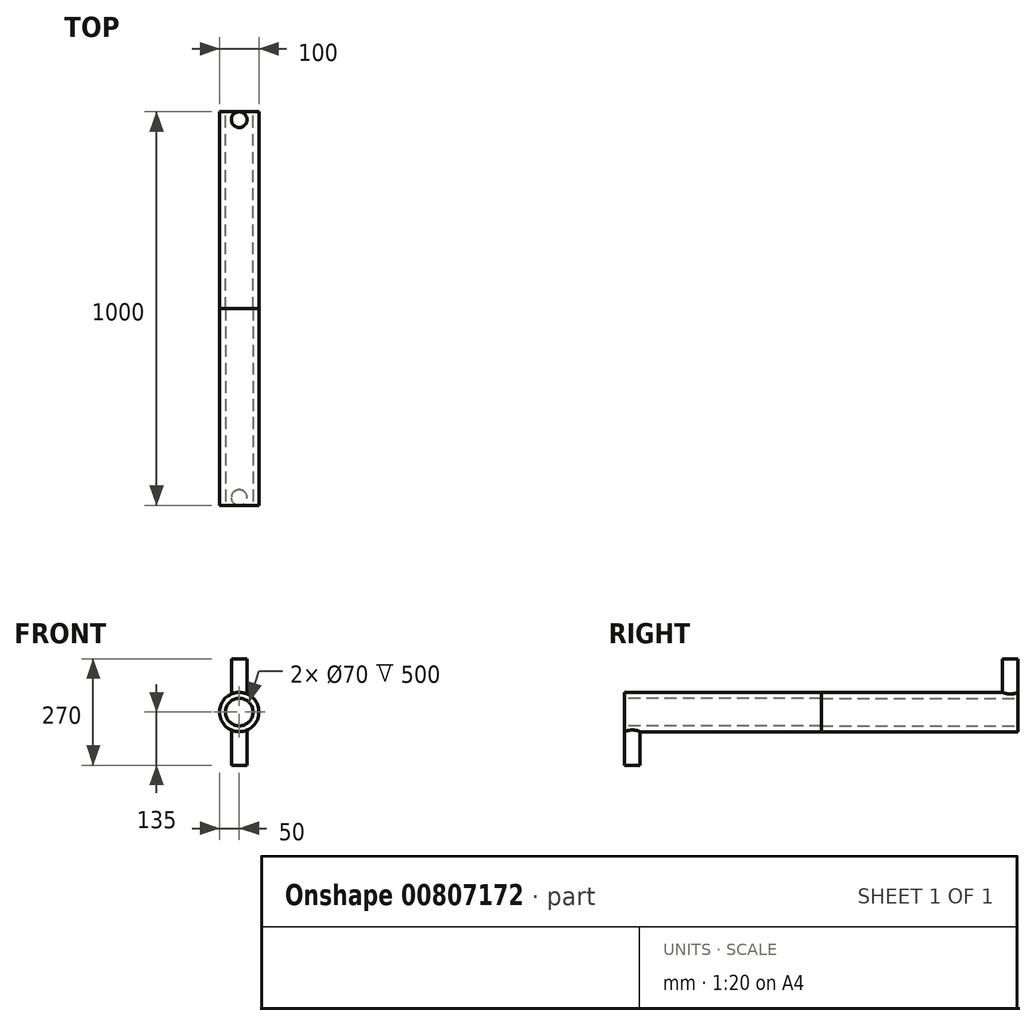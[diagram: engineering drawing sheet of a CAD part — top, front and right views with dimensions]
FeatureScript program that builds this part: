
annotation { "Feature Type Name" : "Feature", "Feature Type Description" : "" }
export const myFeature = defineFeature(function(context is Context, id is Id, definition is map)
    precondition{}
    {
        {
            var Q0;
            Q0=qCreatedBy(makeId("Front.planeOp"),FACE);
            var sketch = newSketch(context, id + "F0", { "sketchPlane" : qUnion([Q0])});
            skCircle(sketch, "E0", {"center": v(0, 0) * mm, "radius": 35 * mm});
            skCircle(sketch, "E1", {"center": v(0, 0) * mm, "radius": 50 * mm});
            skSolve(sketch);
        }
        {
            var Q0;
            Q0=makeQuery(id+"F0.imprint","IMPRINT",FACE,{"disambiguationData":[TD([[makeQuery(id+"F0.imprint","IMPRINT",EDGE,{"derivedFrom":sQuery(id+"F0.wireOp",EDGE,"E0")}),-1.0]])]});
            extrude(context, id + "F1", {"entities" : qUnion([Q0]), "depth" : 500 * mm, "offsetDistance" : 25 * mm});
        }
        {
            var Q0;
            Q0=qCreatedBy(makeId("Top.planeOp"),FACE);
            cPlane(context, id + "F2", {"entities" : qUnion([Q0]), "cplaneType" : CPlaneType.OFFSET, "offset" : 35 * mm, "width" : 150 * mm, "height" : 150 * mm});
        }
        {
            var Q0;
            Q0=qCreatedBy(id+"F2.planeOp",FACE);
            var sketch = newSketch(context, id + "F3", { "sketchPlane" : qUnion([Q0])});
            skCircle(sketch, "E2", {"center": v(0, -20) * mm, "radius": 20 * mm});
            skSolve(sketch);
        }
        {
            var Q0;
            Q0 = qSketchRegion(id + "F3", true);
            extrude(context, id + "F4", {"entities" : qUnion([Q0]), "operationType" : NewBodyOperationType.ADD, "depth" : 100 * mm, "offsetDistance" : 25 * mm});
        }
        {
            var Q0;
            Q0=qCreatedBy(makeId("Front.planeOp"),FACE);
            cPlane(context, id + "F5", {"entities" : qUnion([Q0]), "cplaneType" : CPlaneType.OFFSET, "offset" : 500 * mm, "width" : 150 * mm, "height" : 150 * mm});
        }
        {
            var Q0;
            Q0=makeQuery(id+"F1.opExtrude","SWEPT_BODY",BODY,{"disambiguationData":[OSD([sQuery(id+"F0.wireOp",EDGE,"E0"),sQuery(id+"F0.wireOp",EDGE,"E1")])]});
            var Q1;
            Q1=qCreatedBy(id+"F5.planeOp",FACE);
            mirror(context, id + "F6", {"entities" : qUnion([Q0]), "mirrorPlane" : qUnion([Q1])});
        }
        {
            var Q0;
            Q0=makeQuery(id+"F6.opPattern","COPY",BODY,{"derivedFrom":makeQuery(id+"F1.opExtrude","SWEPT_BODY",BODY,{"disambiguationData":[OSD([sQuery(id+"F0.wireOp",EDGE,"E0"),sQuery(id+"F0.wireOp",EDGE,"E1")])]}),"instanceName":"1"});
            var Q1;
            Q1=qCreatedBy(makeId("Top.planeOp"),FACE);
            mirror(context, id + "F7", {"entities" : qUnion([Q0]), "mirrorPlane" : qUnion([Q1])});
        }
        {
            var Q0;
            Q0=makeQuery(id+"F6.opPattern","COPY",BODY,{"derivedFrom":makeQuery(id+"F1.opExtrude","SWEPT_BODY",BODY,{"disambiguationData":[OSD([sQuery(id+"F0.wireOp",EDGE,"E0"),sQuery(id+"F0.wireOp",EDGE,"E1")])]}),"instanceName":"1"});
            deleteBodies(context, id + "F8", {"entities" : qUnion([Q0])});
        }
    });
